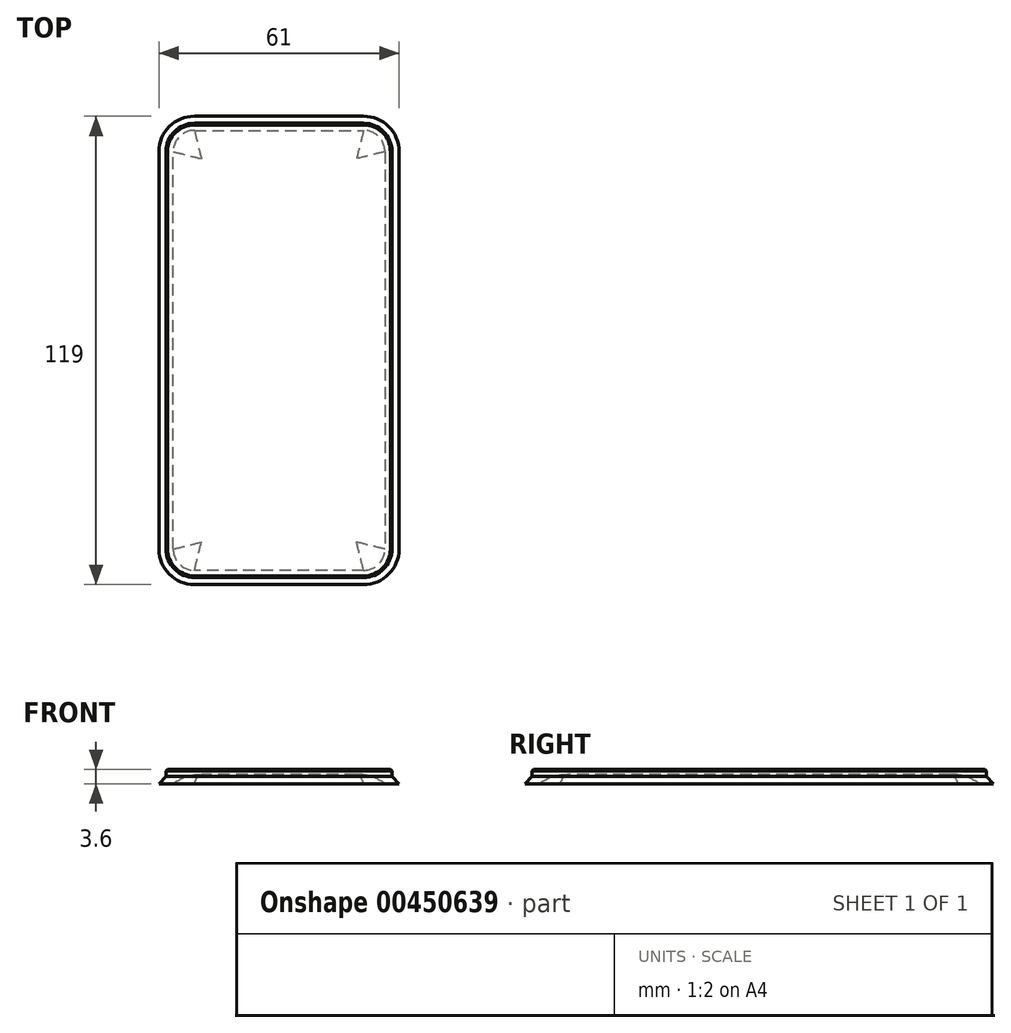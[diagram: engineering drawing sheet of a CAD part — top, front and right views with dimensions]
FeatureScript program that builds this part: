
annotation { "Feature Type Name" : "Feature", "Feature Type Description" : "" }
export const myFeature = defineFeature(function(context is Context, id is Id, definition is map)
    precondition{}
    {
        {
            var Q0;
            Q0=qCreatedBy(makeId("Top.planeOp"),FACE);
            var sketch = newSketch(context, id + "F0", { "sketchPlane" : qUnion([Q0])});
            skPoint(sketch, "E0.middle", {"position": v(0, 0) * mm});
            skLineSegment(sketch, "E1.bottom", {"start": v(30.5, 59.5) * mm, "end": v(-30.5, 59.5) * mm});
            skLineSegment(sketch, "E1.top", {"start": v(30.5, -59.5) * mm, "end": v(-30.5, -59.5) * mm});
            skLineSegment(sketch, "E1.left", {"start": v(30.5, 59.5) * mm, "end": v(30.5, -59.5) * mm});
            skLineSegment(sketch, "E1.right", {"start": v(-30.5, 59.5) * mm, "end": v(-30.5, -59.5) * mm});
            skSolve(sketch);
        }
        {
            var Q0;
            Q0=makeQuery(id+"F0.imprint","IMPRINT",FACE,{"disambiguationData":[TD([[makeQuery(id+"F0.imprint","IMPRINT",EDGE,{"derivedFrom":sQuery(id+"F0.wireOp",EDGE,"E1.bottom")}),1.0]])]});
            extrude(context, id + "F1", {"entities" : qUnion([Q0]), "depth" : 1.8 * mm});
        }
        {
            var Q0;
            Q0=makeQuery(id+"F1.opExtrude","SWEPT_EDGE",EDGE,{"disambiguationData":[OSD([sQuery(id+"F0.wireOp",EDGE,"E1.top"),sQuery(id+"F0.wireOp",EDGE,"E1.right")])]});
            var Q1;
            Q1=makeQuery(id+"F1.opExtrude","SWEPT_EDGE",EDGE,{"disambiguationData":[OSD([sQuery(id+"F0.wireOp",EDGE,"E1.top"),sQuery(id+"F0.wireOp",EDGE,"E1.left")])]});
            var Q2;
            Q2=makeQuery(id+"F1.opExtrude","SWEPT_EDGE",EDGE,{"disambiguationData":[OSD([sQuery(id+"F0.wireOp",EDGE,"E1.bottom"),sQuery(id+"F0.wireOp",EDGE,"E1.right")])]});
            var Q3;
            Q3=makeQuery(id+"F1.opExtrude","SWEPT_EDGE",EDGE,{"disambiguationData":[OSD([sQuery(id+"F0.wireOp",EDGE,"E1.bottom"),sQuery(id+"F0.wireOp",EDGE,"E1.left")])]});
            fillet(context, id + "F2", {"entities" : qUnion([Q0, Q1, Q2, Q3]), "radius" : 9 * mm, "tangentPropagation" : true, "allowEdgeOverflow" : false});
        }
        {
            var Q0;
            {var subQ0=sQuery(id+"F0.wireOp",EDGE,"E1.right");var subQ1=sQuery(id+"F0.wireOp",EDGE,"E1.bottom");Q0=makeQuery(id+"F2.opFillet","BLEND_EDGE",EDGE,{"blendedFrom":[makeQuery(id+"F1.opExtrude","SWEPT_EDGE",EDGE,{"disambiguationData":[OSD([subQ1,subQ0])]}),makeQuery(id+"F1.opExtrude","CAP_FACE",FACE,{"disambiguationData":[OSD([subQ1,sQuery(id+"F0.wireOp",EDGE,"E1.top"),sQuery(id+"F0.wireOp",EDGE,"E1.left"),subQ0])],"isStart":false})],"blendedInto":[makeQuery(id+"F1.opExtrude","CAP_FACE",FACE,{"disambiguationData":[OSD([subQ1,sQuery(id+"F0.wireOp",EDGE,"E1.top"),sQuery(id+"F0.wireOp",EDGE,"E1.left"),subQ0])],"isStart":false})]});}
            chamfer(context, id + "F3", {"entities" : qUnion([Q0]), "width" : 1.8 * mm, "tangentPropagation" : true});
        }
        {
            var Q0;
            Q0=makeQuery(id+"F1.opExtrude","CAP_FACE",FACE,{"disambiguationData":[OSD([sQuery(id+"F0.wireOp",EDGE,"E1.bottom"),sQuery(id+"F0.wireOp",EDGE,"E1.top"),sQuery(id+"F0.wireOp",EDGE,"E1.left"),sQuery(id+"F0.wireOp",EDGE,"E1.right")])],"isStart":false});
            extrude(context, id + "F4", {"entities" : qUnion([Q0]), "operationType" : NewBodyOperationType.ADD, "depth" : 1.8 * mm});
        }
        {
            var Q0;
            Q0=makeQuery(id+"F4.opExtrude","CAP_FACE",FACE,{"disambiguationData":[OSD([sQuery(id+"F0.wireOp",EDGE,"E1.bottom"),sQuery(id+"F0.wireOp",EDGE,"E1.top"),sQuery(id+"F0.wireOp",EDGE,"E1.left"),sQuery(id+"F0.wireOp",EDGE,"E1.right")])],"isStart":false});
            chamfer(context, id + "F5", {"entities" : qUnion([Q0]), "width" : .4 * mm, "tangentPropagation" : true});
        }
        {
            var Q0;
            Q0=makeQuery(id+"F1.opExtrude","CAP_FACE",FACE,{"disambiguationData":[OSD([sQuery(id+"F0.wireOp",EDGE,"E1.bottom"),sQuery(id+"F0.wireOp",EDGE,"E1.top"),sQuery(id+"F0.wireOp",EDGE,"E1.left"),sQuery(id+"F0.wireOp",EDGE,"E1.right")])],"isStart":true});
            var sketch = newSketch(context, id + "F6", { "sketchPlane" : qUnion([Q0])});
            skArc(sketch, "E2.0", {"start": v(21.5, -55.9) * mm, "mid": v(25.32, -54.32) * mm, "end": v(26.9, -50.5) * mm});
            skLineSegment(sketch, "E2.1", {"start": v(-21.5, -55.9) * mm, "end": v(21.5, -55.9) * mm});
            skLineSegment(sketch, "E2.2", {"start": v(26.9, -50.5) * mm, "end": v(26.9, 50.5) * mm});
            skArc(sketch, "E2.3", {"start": v(-26.9, -50.5) * mm, "mid": v(-25.32, -54.32) * mm, "end": v(-21.5, -55.9) * mm});
            skArc(sketch, "E2.4", {"start": v(26.9, 50.5) * mm, "mid": v(25.32, 54.32) * mm, "end": v(21.5, 55.9) * mm});
            skLineSegment(sketch, "E2.5", {"start": v(21.5, 55.9) * mm, "end": v(-21.5, 55.9) * mm});
            skArc(sketch, "E2.6", {"start": v(-21.5, 55.9) * mm, "mid": v(-25.32, 54.32) * mm, "end": v(-26.9, 50.5) * mm});
            skLineSegment(sketch, "E2.7", {"start": v(-26.9, 50.5) * mm, "end": v(-26.9, -50.5) * mm});
            skSolve(sketch);
        }
        {
            var Q0;
            Q0=makeQuery(id+"F6.imprint","IMPRINT",FACE,{"disambiguationData":[TD([[makeQuery(id+"F6.imprint","IMPRINT",EDGE,{"derivedFrom":sQuery(id+"F6.wireOp",EDGE,"E2.0")}),1.0]])]});
            extrude(context, id + "F7", {"entities" : qUnion([Q0]), "operationType" : NewBodyOperationType.REMOVE, "oppositeDirection" : true, "depth" : 2.4 * mm});
        }
        {
            var Q0;
            Q0=makeQuery(id+"F7.boolean.opBoolean","COPY",FACE,{"derivedFrom":makeQuery(id+"F7.opExtrude","CAP_FACE",FACE,{"disambiguationData":[OSD([sQuery(id+"F6.wireOp",EDGE,"E2.0"),sQuery(id+"F6.wireOp",EDGE,"E2.1"),sQuery(id+"F6.wireOp",EDGE,"E2.2"),sQuery(id+"F6.wireOp",EDGE,"E2.3"),sQuery(id+"F6.wireOp",EDGE,"E2.4"),sQuery(id+"F6.wireOp",EDGE,"E2.5"),sQuery(id+"F6.wireOp",EDGE,"E2.6"),sQuery(id+"F6.wireOp",EDGE,"E2.7")])],"isStart":false})});
            fillet(context, id + "F8", {"entities" : qUnion([Q0]), "radius" : 12 * mm, "tangentPropagation" : true, "allowEdgeOverflow" : false});
        }
    });
